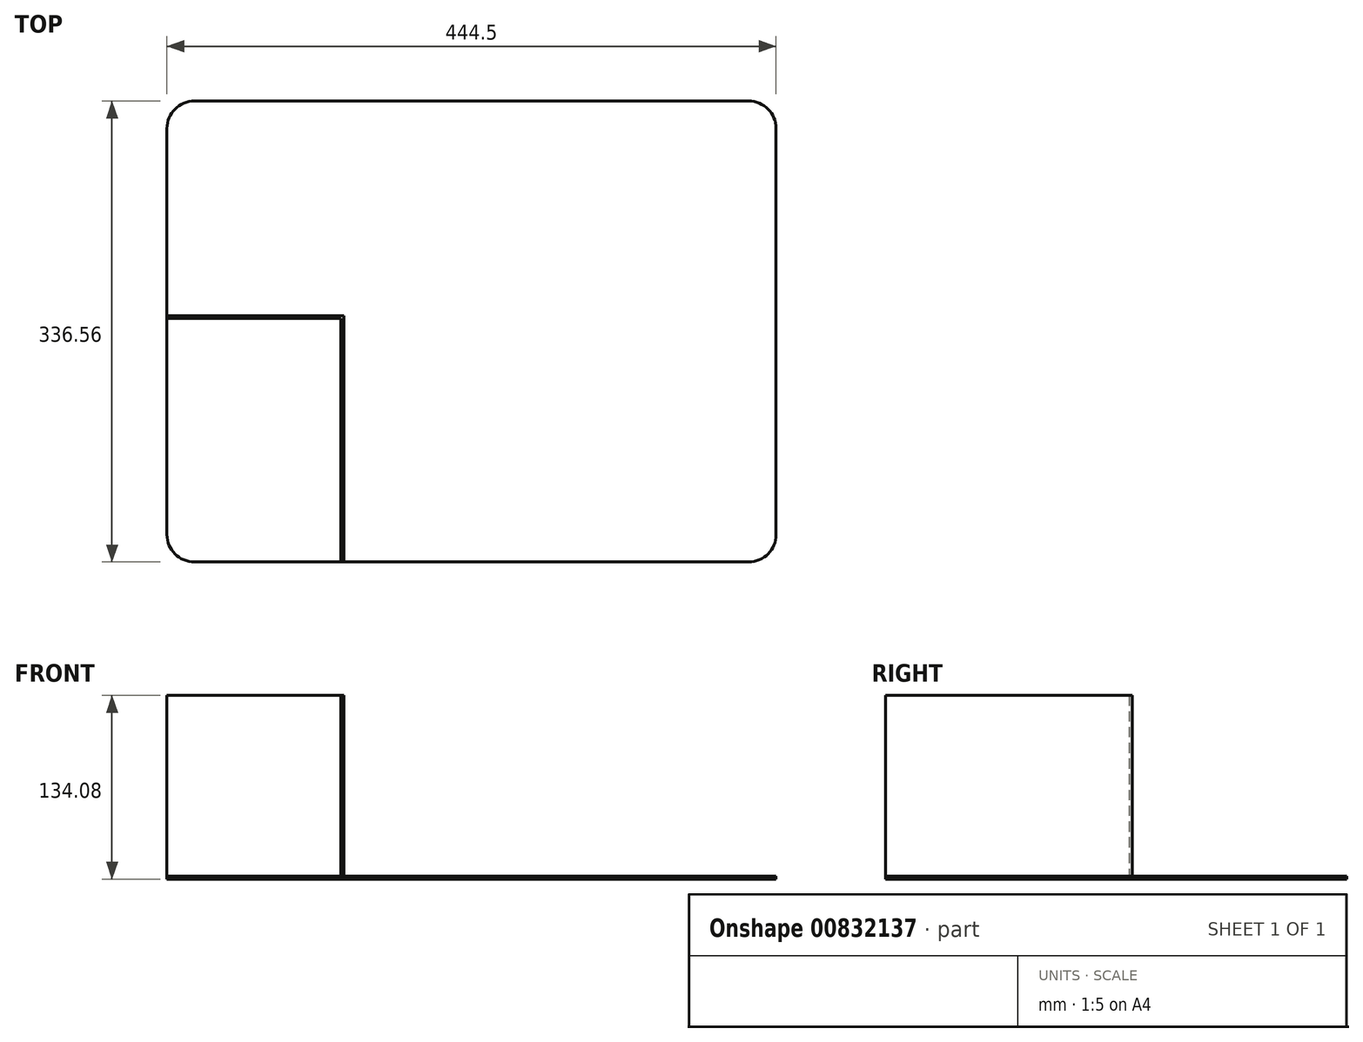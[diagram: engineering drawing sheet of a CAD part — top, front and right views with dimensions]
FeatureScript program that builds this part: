
annotation { "Feature Type Name" : "Feature", "Feature Type Description" : "" }
export const myFeature = defineFeature(function(context is Context, id is Id, definition is map)
    precondition{}
    {
        {
            var Q0;
            Q0=qCreatedBy(makeId("Top.planeOp"),FACE);
            var sketch = newSketch(context, id + "F0", { "sketchPlane" : qUnion([Q0])});
            skLineSegment(sketch, "E0.bottom", {"start": v(222.25, -168.27) * mm, "end": v(-222.25, -168.28) * mm});
            skLineSegment(sketch, "E0.top", {"start": v(222.25, 168.28) * mm, "end": v(-222.25, 168.28) * mm});
            skLineSegment(sketch, "E0.left", {"start": v(222.25, -168.28) * mm, "end": v(222.25, 168.28) * mm});
            skLineSegment(sketch, "E0.right", {"start": v(-222.25, -168.28) * mm, "end": v(-222.25, 168.28) * mm});
            skPoint(sketch, "E0.middle", {"position": v(0, 0) * mm});
            skSolve(sketch);
        }
        {
            var Q0;
            Q0 = qSketchRegion(id + "F0", true);
            extrude(context, id + "F1", {"entities" : qUnion([Q0]), "depth" : 2 * mm, "offsetDistance" : 25.4 * mm});
        }
        {
            var Q0;
            Q0=makeQuery(id+"F1.opExtrude","CAP_FACE",FACE,{"disambiguationData":[OSD([sQuery(id+"F0.wireOp",EDGE,"E0.bottom"),sQuery(id+"F0.wireOp",EDGE,"E0.top"),sQuery(id+"F0.wireOp",EDGE,"E0.left"),sQuery(id+"F0.wireOp",EDGE,"E0.right")])],"isStart":false});
            var sketch = newSketch(context, id + "F2", { "sketchPlane" : qUnion([Q0])});
            skLineSegment(sketch, "E1", {"start": v(-222.25, 9.52) * mm, "end": v(-95.25, 9.52) * mm});
            skLineSegment(sketch, "E2", {"start": v(-95.25, 9.52) * mm, "end": v(-95.25, -168.28) * mm});
            skLineSegment(sketch, "E3", {"start": v(-222.25, 9.52) * mm, "end": v(-222.25, 11.52) * mm});
            skLineSegment(sketch, "E4", {"start": v(-95.25, -168.28) * mm, "end": v(-93.25, -168.28) * mm});
            skLineSegment(sketch, "E5", {"start": v(-93.25, -168.28) * mm, "end": v(-93.25, 11.52) * mm});
            skLineSegment(sketch, "E6", {"start": v(-93.25, 11.52) * mm, "end": v(-222.25, 11.52) * mm});
            skSolve(sketch);
        }
        {
            var Q0;
            Q0 = qSketchRegion(id + "F2", true);
            extrude(context, id + "F3", {"entities" : qUnion([Q0]), "depth" : 132.08 * mm, "offsetDistance" : 25.4 * mm});
        }
        {
            var Q0;
            Q0=makeQuery(id+"F1.opExtrude","SWEPT_EDGE",EDGE,{"disambiguationData":[OSD([sQuery(id+"F0.wireOp",EDGE,"E0.bottom"),sQuery(id+"F0.wireOp",EDGE,"E0.left")])]});
            var Q1;
            Q1=makeQuery(id+"F1.opExtrude","SWEPT_EDGE",EDGE,{"disambiguationData":[OSD([sQuery(id+"F0.wireOp",EDGE,"E0.bottom"),sQuery(id+"F0.wireOp",EDGE,"E0.right")])]});
            var Q2;
            Q2=makeQuery(id+"F1.opExtrude","SWEPT_EDGE",EDGE,{"disambiguationData":[OSD([sQuery(id+"F0.wireOp",EDGE,"E0.top"),sQuery(id+"F0.wireOp",EDGE,"E0.right")])]});
            var Q3;
            Q3=makeQuery(id+"F1.opExtrude","SWEPT_EDGE",EDGE,{"disambiguationData":[OSD([sQuery(id+"F0.wireOp",EDGE,"E0.top"),sQuery(id+"F0.wireOp",EDGE,"E0.left")])]});
            fillet(context, id + "F4", {"entities" : qUnion([Q0, Q1, Q2, Q3]), "radius" : 20 * mm, "tangentPropagation" : true, "allowEdgeOverflow" : false});
        }
    });
